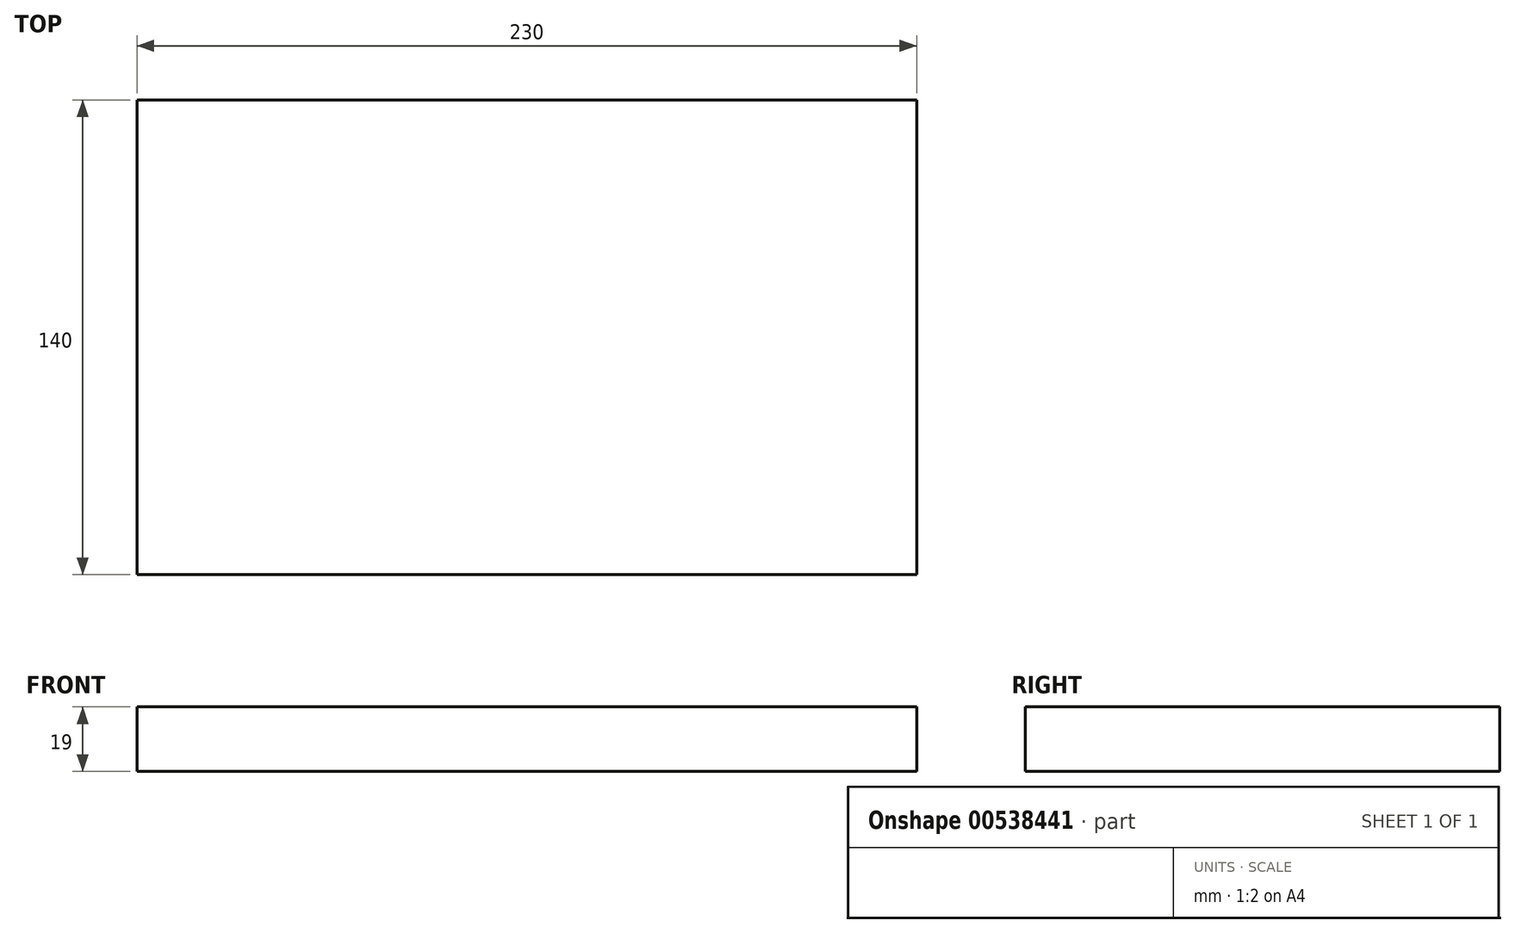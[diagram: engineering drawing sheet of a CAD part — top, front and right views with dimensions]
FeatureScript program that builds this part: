
annotation { "Feature Type Name" : "Feature", "Feature Type Description" : "" }
export const myFeature = defineFeature(function(context is Context, id is Id, definition is map)
    precondition{}
    {
        {
            var Q0;
            Q0=qCreatedBy(makeId("Top.planeOp"),FACE);
            var sketch = newSketch(context, id + "F0", { "sketchPlane" : qUnion([Q0])});
            skLineSegment(sketch, "E0.bottom", {"start": v(115, -70) * mm, "end": v(-115, -70) * mm});
            skLineSegment(sketch, "E0.top", {"start": v(115, 70) * mm, "end": v(-115, 70) * mm});
            skLineSegment(sketch, "E0.left", {"start": v(115, -70) * mm, "end": v(115, 70) * mm});
            skLineSegment(sketch, "E0.right", {"start": v(-115, -70) * mm, "end": v(-115, 70) * mm});
            skPoint(sketch, "E0.middle", {"position": v(0, 0) * mm});
            skSolve(sketch);
        }
        {
            var Q0;
            Q0=makeQuery(id+"F0.imprint","IMPRINT",FACE,{"disambiguationData":[TD([[makeQuery(id+"F0.imprint","IMPRINT",EDGE,{"derivedFrom":sQuery(id+"F0.wireOp",EDGE,"E0.bottom")}),-1.0]])]});
            extrude(context, id + "F1", {"entities" : qUnion([Q0]), "depth" : 19 * mm, "offsetDistance" : 25 * mm});
        }
    });
